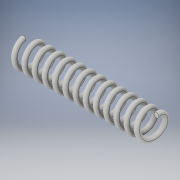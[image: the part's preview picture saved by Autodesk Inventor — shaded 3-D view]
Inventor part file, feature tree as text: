
AUTODESK INVENTOR PART (.ipt)
format: ipt  version: 2018.3 (Build 223284000, 284)  size: 350,208 bytes
history: native  units: in
note: dims shown in document units (in); Inventor stores cm internally (conversion verified against a paired STEP export)
features: helix x1, sketch x1
ambient origin geometry x8: Origin, YZ Plane, XZ Plane, XY Plane, X Axis, Y Axis, Z Axis, Center Point
bodies: Solid1 (feature_tree)
feature tree (2):
  helix  "Coil1"  [1 undecoded]
  sketch  "Sketch1"  dims[d1=0.149in d2=0.026in d3=1.0in d4=0.708in d5=5.1181in d6=0.0in d7=90.0deg d8=90.0deg d9=0.0in d10=0.0in]
note: 1 required parameter value undecoded (feature->parameter linkage not recoverable at this tier; creation-order binding heuristic only, values carry confidence <= 0.55)
